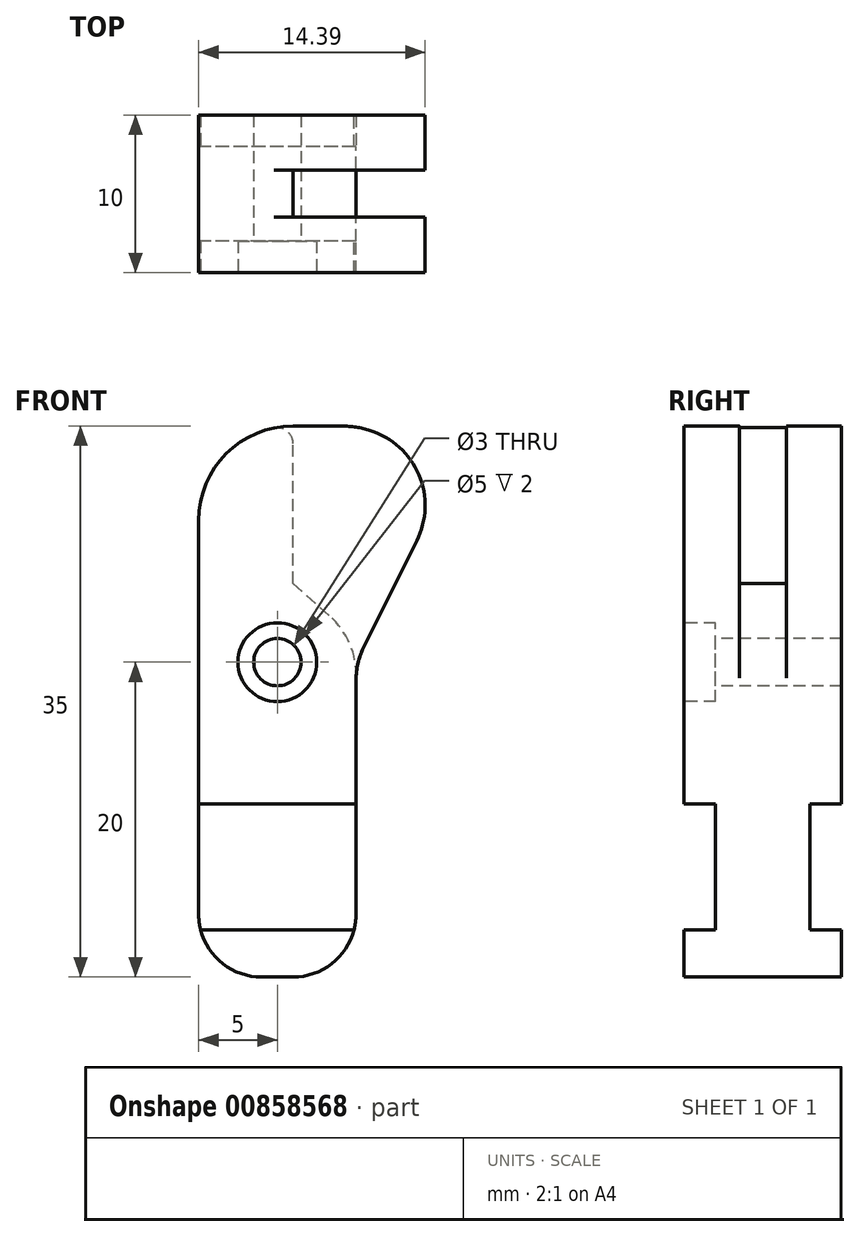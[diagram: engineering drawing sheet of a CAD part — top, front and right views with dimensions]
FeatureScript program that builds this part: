
annotation { "Feature Type Name" : "Feature", "Feature Type Description" : "" }
export const myFeature = defineFeature(function(context is Context, id is Id, definition is map)
    precondition{}
    {
        {
            var Q0;
            Q0=qCreatedBy(makeId("Front.planeOp"),FACE);
            var sketch = newSketch(context, id + "F0", { "sketchPlane" : qUnion([Q0])});
            skLineSegment(sketch, "E0", {"start": v(0, 0) * mm, "end": v(0, 35) * mm});
            skLineSegment(sketch, "E1", {"start": v(0, 35) * mm, "end": v(15, 35) * mm});
            skLineSegment(sketch, "E2", {"start": v(15, 35) * mm, "end": v(15, 30) * mm});
            skLineSegment(sketch, "E3", {"start": v(0, 0) * mm, "end": v(10, 0) * mm});
            skLineSegment(sketch, "E4", {"start": v(10, 0) * mm, "end": v(10, 20) * mm});
            skLineSegment(sketch, "E5", {"start": v(10, 20) * mm, "end": v(15, 30) * mm});
            skSolve(sketch);
        }
        {
            var Q0;
            Q0 = qSketchRegion(id + "F0", true);
            extrude(context, id + "F1", {"entities" : qUnion([Q0]), "depth" : 10 * mm, "offsetDistance" : 25 * mm});
        }
        {
            var Q0;
            Q0=makeQuery(id+"F1.opExtrude","SWEPT_FACE",FACE,{"disambiguationData":[OSD([sQuery(id+"F0.wireOp",EDGE,"E0")])]});
            var sketch = newSketch(context, id + "F2", { "sketchPlane" : qUnion([Q0])});
            skLineSegment(sketch, "E6", {"start": v(0, 0) * mm, "end": v(0, 3) * mm});
            skLineSegment(sketch, "E7", {"start": v(0, 3) * mm, "end": v(0, 11) * mm});
            skLineSegment(sketch, "E8", {"start": v(0, 11) * mm, "end": v(2, 11) * mm});
            skLineSegment(sketch, "E9", {"start": v(2, 11) * mm, "end": v(2, 3) * mm});
            skLineSegment(sketch, "E10", {"start": v(2, 3) * mm, "end": v(0, 3) * mm});
            skLineSegment(sketch, "E11", {"start": v(2, 3) * mm, "end": v(10, 3) * mm});
            skLineSegment(sketch, "E12", {"start": v(10, 3) * mm, "end": v(10, 11) * mm});
            skLineSegment(sketch, "E13", {"start": v(10, 11) * mm, "end": v(8, 11) * mm});
            skLineSegment(sketch, "E14", {"start": v(8, 11) * mm, "end": v(8, 3) * mm});
            skSolve(sketch);
        }
        {
            var Q0;
            Q0 = qSketchRegion(id + "F2", true);
            extrude(context, id + "F3", {"entities" : qUnion([Q0]), "operationType" : NewBodyOperationType.REMOVE, "oppositeDirection" : true, "depth" : 25 * mm, "offsetDistance" : 25 * mm});
        }
        {
            var Q0;
            Q0=makeQuery(id+"F1.opExtrude","SWEPT_EDGE",EDGE,{"disambiguationData":[OSD([sQuery(id+"F0.wireOp",EDGE,"E0"),sQuery(id+"F0.wireOp",EDGE,"E1")])]});
            var Q1;
            Q1=makeQuery(id+"F1.opExtrude","SWEPT_EDGE",EDGE,{"disambiguationData":[OSD([sQuery(id+"F0.wireOp",EDGE,"E1"),sQuery(id+"F0.wireOp",EDGE,"E2")])]});
            fillet(context, id + "F4", {"entities" : qUnion([Q0, Q1]), "radius" : 6 * mm, "tangentPropagation" : true, "allowEdgeOverflow" : false});
        }
        {
            var Q0;
            Q0=makeQuery(id+"F1.opExtrude","SWEPT_EDGE",EDGE,{"disambiguationData":[OSD([sQuery(id+"F0.wireOp",EDGE,"E0"),sQuery(id+"F0.wireOp",EDGE,"E3")])]});
            var Q1;
            Q1=makeQuery(id+"F1.opExtrude","SWEPT_EDGE",EDGE,{"disambiguationData":[OSD([sQuery(id+"F0.wireOp",EDGE,"E3"),sQuery(id+"F0.wireOp",EDGE,"E4")])]});
            fillet(context, id + "F5", {"entities" : qUnion([Q0, Q1]), "radius" : 4 * mm, "tangentPropagation" : true, "allowEdgeOverflow" : false});
        }
        {
            var Q0;
            {var subQ0=sQuery(id+"F0.wireOp",EDGE,"E4");var subQ1=sQuery(id+"F0.wireOp",EDGE,"E2");var subQ2=sQuery(id+"F0.wireOp",EDGE,"E1");var subQ3=sQuery(id+"F0.wireOp",EDGE,"E0");var subQ4=sQuery(id+"F0.wireOp",EDGE,"E5");Q0=makeQuery(id+"F3.boolean.opBoolean","SPLIT",FACE,{"disambiguationData":[TD([makeQuery(id+"F1.opExtrude","SWEPT_FACE",FACE,{"disambiguationData":[OSD([subQ2])]})])],"derivedFrom":makeQuery(id+"F1.opExtrude","CAP_FACE",FACE,{"disambiguationData":[OSD([subQ3,subQ2,subQ1,sQuery(id+"F0.wireOp",EDGE,"E3"),subQ0,subQ4])],"isStart":false})});}
            var sketch = newSketch(context, id + "F6", { "sketchPlane" : qUnion([Q0])});
            skLineSegment(sketch, "E15", {"start": v(5, 11) * mm, "end": v(5, 0) * mm});
            skLineSegment(sketch, "E16", {"start": v(5, 0) * mm, "end": v(5, 20) * mm});
            skCircle(sketch, "E17", {"center": v(5, 20) * mm, "radius": 1.5 * mm});
            skSolve(sketch);
        }
        {
            var Q0;
            Q0 = qSketchRegion(id + "F6", true);
            extrude(context, id + "F7", {"entities" : qUnion([Q0]), "operationType" : NewBodyOperationType.REMOVE, "oppositeDirection" : true, "depth" : 25 * mm, "offsetDistance" : 25 * mm});
        }
        {
            var Q0;
            {var subQ0=sQuery(id+"F0.wireOp",EDGE,"E4");var subQ1=sQuery(id+"F0.wireOp",EDGE,"E2");var subQ2=sQuery(id+"F0.wireOp",EDGE,"E1");var subQ3=sQuery(id+"F0.wireOp",EDGE,"E0");var subQ4=sQuery(id+"F0.wireOp",EDGE,"E5");Q0=makeQuery(id+"F3.boolean.opBoolean","SPLIT",FACE,{"disambiguationData":[TD([makeQuery(id+"F1.opExtrude","SWEPT_FACE",FACE,{"disambiguationData":[OSD([subQ2])]})])],"derivedFrom":makeQuery(id+"F1.opExtrude","CAP_FACE",FACE,{"disambiguationData":[OSD([subQ3,subQ2,subQ1,sQuery(id+"F0.wireOp",EDGE,"E3"),subQ0,subQ4])],"isStart":false})});}
            var sketch = newSketch(context, id + "F8", { "sketchPlane" : qUnion([Q0])});
            skCircle(sketch, "E18", {"center": v(5, 20) * mm, "radius": 2.5 * mm});
            skSolve(sketch);
        }
        {
            var Q0;
            Q0 = qSketchRegion(id + "F8", true);
            extrude(context, id + "F9", {"entities" : qUnion([Q0]), "operationType" : NewBodyOperationType.REMOVE, "oppositeDirection" : true, "depth" : 2 * mm, "offsetDistance" : 25 * mm});
        }
        {
            var Q0;
            Q0=makeQuery(id+"F1.opExtrude","SWEPT_EDGE",EDGE,{"disambiguationData":[OSD([sQuery(id+"F0.wireOp",EDGE,"E2"),sQuery(id+"F0.wireOp",EDGE,"E5")])]});
            var Q1;
            Q1=makeQuery(id+"F1.opExtrude","SWEPT_EDGE",EDGE,{"disambiguationData":[OSD([sQuery(id+"F0.wireOp",EDGE,"E4"),sQuery(id+"F0.wireOp",EDGE,"E5")])]});
            fillet(context, id + "F10", {"entities" : qUnion([Q0, Q1]), "radius" : 5 * mm, "tangentPropagation" : true, "allowEdgeOverflow" : false});
        }
        {
            var Q0;
            Q0=makeQuery(id+"F4.opFillet","BLEND_EDGE",EDGE,{"blendedFrom":[makeQuery(id+"F1.opExtrude","SWEPT_EDGE",EDGE,{"disambiguationData":[OSD([sQuery(id+"F0.wireOp",EDGE,"E1"),sQuery(id+"F0.wireOp",EDGE,"E2")])]}),makeQuery(id+"F1.opExtrude","SWEPT_FACE",FACE,{"disambiguationData":[OSD([sQuery(id+"F0.wireOp",EDGE,"E5")])]})],"blendedInto":[makeQuery(id+"F1.opExtrude","SWEPT_FACE",FACE,{"disambiguationData":[OSD([sQuery(id+"F0.wireOp",EDGE,"E5")])]})]});
            fillet(context, id + "F11", {"entities" : qUnion([Q0]), "radius" : 5 * mm, "tangentPropagation" : true, "allowEdgeOverflow" : false});
        }
        {
            var Q0;
            Q0=makeQuery(id+"F1.opExtrude","SWEPT_FACE",FACE,{"disambiguationData":[OSD([sQuery(id+"F0.wireOp",EDGE,"E1")])]});
            var sketch = newSketch(context, id + "F12", { "sketchPlane" : qUnion([Q0])});
            skLineSegment(sketch, "E19", {"start": v(6, -5) * mm, "end": v(6, -3.5) * mm});
            skLineSegment(sketch, "E20", {"start": v(6, -3.5) * mm, "end": v(19.67, -3.5) * mm});
            skLineSegment(sketch, "E21", {"start": v(19.67, -3.5) * mm, "end": v(19.93, -6.49) * mm});
            skLineSegment(sketch, "E22", {"start": v(19.93, -6.49) * mm, "end": v(6, -6.49) * mm});
            skLineSegment(sketch, "E23", {"start": v(6, -6.49) * mm, "end": v(6, -5) * mm});
            skSolve(sketch);
        }
        {
            var Q0;
            Q0 = qSketchRegion(id + "F12", true);
            extrude(context, id + "F13", {"entities" : qUnion([Q0]), "operationType" : NewBodyOperationType.REMOVE, "oppositeDirection" : true, "depth" : 10 * mm, "offsetDistance" : 25 * mm});
        }
        {
            var Q0;
            Q0=makeQuery(id+"F13.boolean.opBoolean","INTERSECT",EDGE,{"derivedFrom":[makeQuery(id+"F1.opExtrude","SWEPT_FACE",FACE,{"disambiguationData":[OSD([sQuery(id+"F0.wireOp",EDGE,"E5")])]}),makeQuery(id+"F13.opExtrude","CAP_FACE",FACE,{"disambiguationData":[OSD([sQuery(id+"F12.wireOp",EDGE,"E19"),sQuery(id+"F12.wireOp",EDGE,"E20"),sQuery(id+"F12.wireOp",EDGE,"E21"),sQuery(id+"F12.wireOp",EDGE,"E22"),sQuery(id+"F12.wireOp",EDGE,"E23")])],"isStart":false})]});
            chamfer(context, id + "F14", {"entities" : qUnion([Q0]), "chamferType" : ChamferType.TWO_OFFSETS, "width1" : 6.5 * mm, "oppositeDirection" : false, "width2" : 4.5 * mm, "tangentPropagation" : true});
        }
        {
            var Q0;
            {var subQ0=sQuery(id+"F0.wireOp",EDGE,"E5");Q0=makeQuery(id+"F14.opChamfer","BLEND_EDGE",EDGE,{"blendedFrom":[makeQuery(id+"F13.boolean.opBoolean","INTERSECT",EDGE,{"derivedFrom":[makeQuery(id+"F1.opExtrude","SWEPT_FACE",FACE,{"disambiguationData":[OSD([subQ0])]}),makeQuery(id+"F13.opExtrude","CAP_FACE",FACE,{"disambiguationData":[OSD([sQuery(id+"F12.wireOp",EDGE,"E19"),sQuery(id+"F12.wireOp",EDGE,"E20"),sQuery(id+"F12.wireOp",EDGE,"E21"),sQuery(id+"F12.wireOp",EDGE,"E22"),sQuery(id+"F12.wireOp",EDGE,"E23")])],"isStart":false})]}),makeQuery(id+"F10.opFillet","BLEND_FACE",FACE,{"disambiguationData":[OSD([sQuery(id+"F0.wireOp",EDGE,"E4"),subQ0])]})],"blendedInto":[makeQuery(id+"F10.opFillet","BLEND_FACE",FACE,{"disambiguationData":[OSD([sQuery(id+"F0.wireOp",EDGE,"E4"),subQ0])]})]});}
            fillet(context, id + "F15", {"entities" : qUnion([Q0]), "radius" : 5 * mm, "tangentPropagation" : true, "allowEdgeOverflow" : false});
        }
        {
            var Q0;
            {var subQ0=sQuery(id+"F0.wireOp",EDGE,"E1");Q0=makeQuery(id+"F13.boolean.opBoolean","MERGE",EDGE,{"derivedFrom":[makeQuery(id+"F4.opFillet","BLEND_EDGE",EDGE,{"blendedFrom":[makeQuery(id+"F1.opExtrude","SWEPT_EDGE",EDGE,{"disambiguationData":[OSD([sQuery(id+"F0.wireOp",EDGE,"E0"),subQ0])]}),makeQuery(id+"F1.opExtrude","SWEPT_FACE",FACE,{"disambiguationData":[OSD([subQ0])]})],"blendedInto":[makeQuery(id+"F1.opExtrude","SWEPT_FACE",FACE,{"disambiguationData":[OSD([subQ0])]})]}),makeQuery(id+"F13.opExtrude","CAP_EDGE",EDGE,{"disambiguationData":[OSD([sQuery(id+"F12.wireOp",EDGE,"E19"),sQuery(id+"F12.wireOp",EDGE,"E23")])],"isStart":true})]});}
            fillet(context, id + "F16", {"entities" : qUnion([Q0]), "radius" : 1 * mm, "tangentPropagation" : true, "allowEdgeOverflow" : false});
        }
    });
